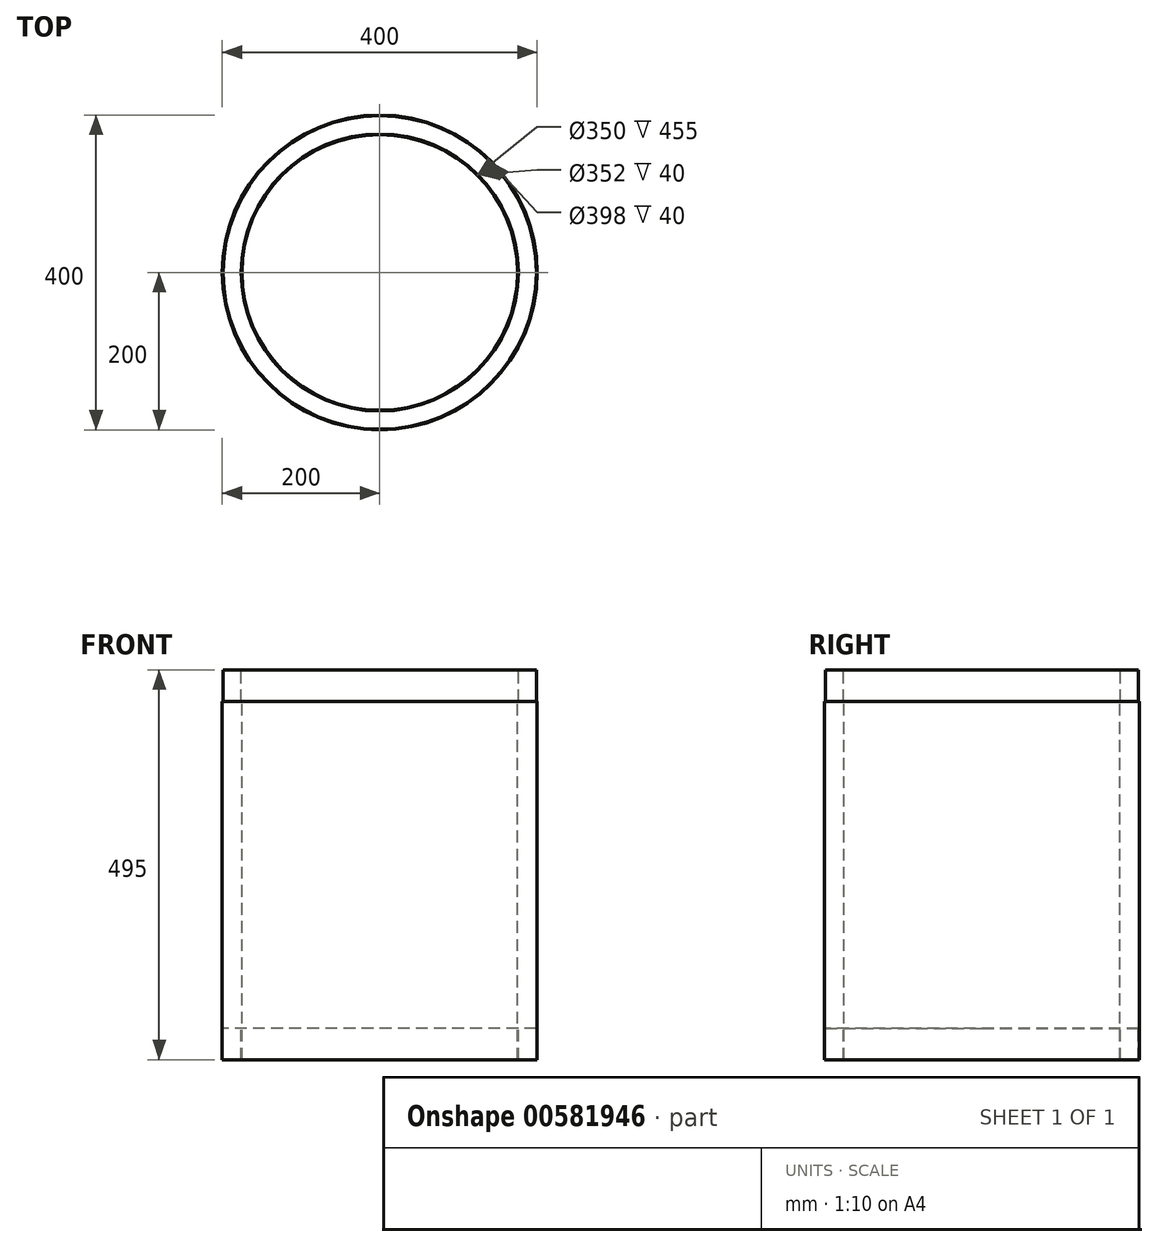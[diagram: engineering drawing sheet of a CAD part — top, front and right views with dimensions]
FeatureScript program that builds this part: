
annotation { "Feature Type Name" : "Feature", "Feature Type Description" : "" }
export const myFeature = defineFeature(function(context is Context, id is Id, definition is map)
    precondition{}
    {
        {
            var Q0;
            Q0=qCreatedBy(makeId("Front.planeOp"),FACE);
            var sketch = newSketch(context, id + "F0", { "sketchPlane" : qUnion([Q0])});
            skLineSegment(sketch, "E0", {"start": v(0, 345.75) * mm, "end": v(0, -558.03) * mm, "construction": true});
            skLineSegment(sketch, "E1", {"start": v(-175, -518.84) * mm, "end": v(-175, -63.84) * mm});
            skLineSegment(sketch, "E2", {"start": v(-175, -63.84) * mm, "end": v(-176, -63.84) * mm});
            skLineSegment(sketch, "E3", {"start": v(-176, -63.84) * mm, "end": v(-176, -23.84) * mm});
            skLineSegment(sketch, "E4", {"start": v(-176, -23.84) * mm, "end": v(-199, -23.84) * mm});
            skLineSegment(sketch, "E5", {"start": v(-199, -23.84) * mm, "end": v(-199, -63.84) * mm});
            skLineSegment(sketch, "E6", {"start": v(-199, -63.84) * mm, "end": v(-200, -63.84) * mm});
            skLineSegment(sketch, "E7", {"start": v(-200, -63.84) * mm, "end": v(-200, -518.84) * mm});
            skLineSegment(sketch, "E8", {"start": v(-200, -518.84) * mm, "end": v(-199, -518.84) * mm});
            skLineSegment(sketch, "E9", {"start": v(-199, -518.84) * mm, "end": v(-199, -478.84) * mm});
            skLineSegment(sketch, "E10", {"start": v(-199, -478.84) * mm, "end": v(-176, -478.84) * mm});
            skLineSegment(sketch, "E11", {"start": v(-176, -478.84) * mm, "end": v(-176, -518.84) * mm});
            skLineSegment(sketch, "E12", {"start": v(-176, -518.84) * mm, "end": v(-175, -518.84) * mm});
            skSolve(sketch);
        }
        {
            var Q0;
            Q0=qSketchRegion(id+"F0",true);
            var Q1;
            Q1=sQuery(id+"F0.wireOp",EDGE,"E0");
            revolve(context, id + "F1", {"entities" : qUnion([Q0]), "axis" : qUnion([Q1]), "revolveType" : RevolveType.FULL});
        }
    });
